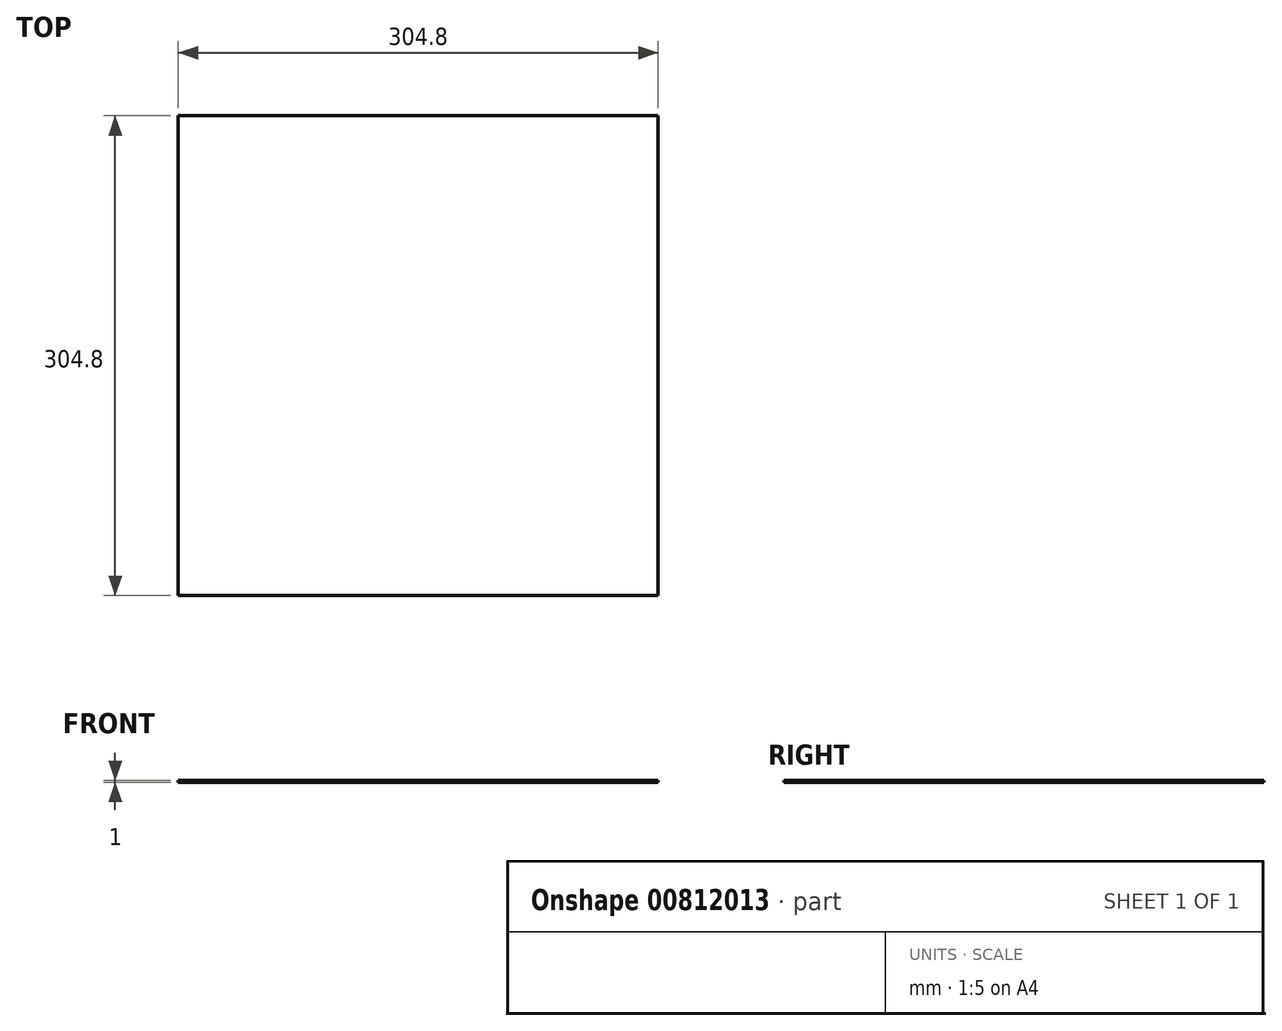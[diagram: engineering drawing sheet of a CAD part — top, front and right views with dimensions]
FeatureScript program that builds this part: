
annotation { "Feature Type Name" : "Feature", "Feature Type Description" : "" }
export const myFeature = defineFeature(function(context is Context, id is Id, definition is map)
    precondition{}
    {
        {
            var Q0;
            Q0=qCreatedBy(makeId("Top.planeOp"),FACE);
            var sketch = newSketch(context, id + "F0", { "sketchPlane" : qUnion([Q0])});
            skLineSegment(sketch, "E0.bottom", {"start": v(-152.4, 152.4) * mm, "end": v(152.4, 152.4) * mm});
            skLineSegment(sketch, "E0.top", {"start": v(-152.4, -152.4) * mm, "end": v(152.4, -152.4) * mm});
            skLineSegment(sketch, "E0.left", {"start": v(-152.4, 152.4) * mm, "end": v(-152.4, -152.4) * mm});
            skLineSegment(sketch, "E0.right", {"start": v(152.4, 152.4) * mm, "end": v(152.4, -152.4) * mm});
            skLineSegment(sketch, "E1", {"start": v(-152.4, 152.4) * mm, "end": v(152.4, -152.4) * mm, "construction": true});
            skSolve(sketch);
        }
        {
            var Q0;
            Q0=makeQuery(id+"F0.imprint","IMPRINT",FACE,{"disambiguationData":[TD([[makeQuery(id+"F0.imprint","IMPRINT",EDGE,{"derivedFrom":sQuery(id+"F0.wireOp",EDGE,"E0.bottom")}),-1.0]])]});
            extrude(context, id + "F1", {"entities" : qUnion([Q0]), "depth" : 1 * mm, "offsetDistance" : 25.4 * mm});
        }
    });
